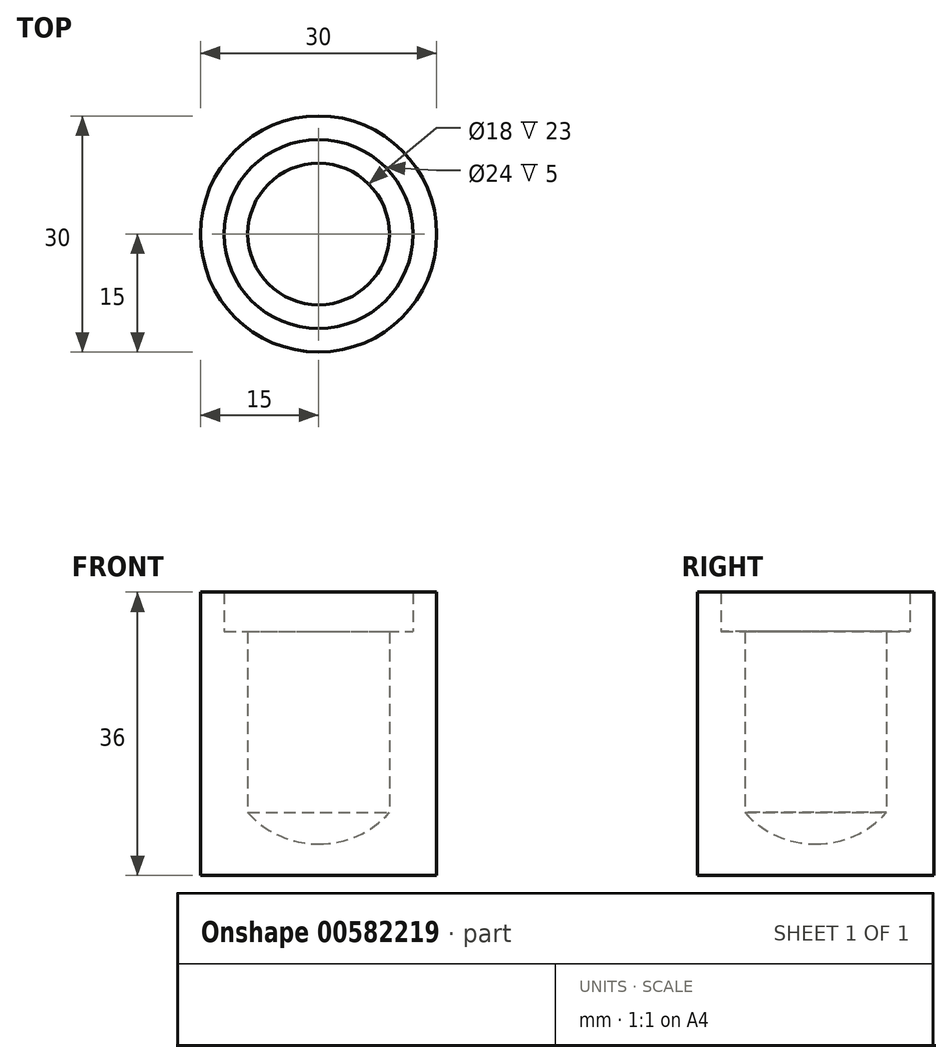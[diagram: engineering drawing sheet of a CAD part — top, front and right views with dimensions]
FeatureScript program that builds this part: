
annotation { "Feature Type Name" : "Feature", "Feature Type Description" : "" }
export const myFeature = defineFeature(function(context is Context, id is Id, definition is map)
    precondition{}
    {
        {
            var Q0;
            Q0=qCreatedBy(makeId("Front.planeOp"),FACE);
            var sketch = newSketch(context, id + "F0", { "sketchPlane" : qUnion([Q0])});
            skLineSegment(sketch, "E0.top", {"start": v(15, -4) * mm, "end": v(-15, -4) * mm});
            skLineSegment(sketch, "E0.left", {"start": v(15, 4) * mm, "end": v(15, -4) * mm});
            skLineSegment(sketch, "E0.right", {"start": v(-15, 4) * mm, "end": v(-15, -4) * mm});
            skPoint(sketch, "E0.middle", {"position": v(0, 0) * mm});
            skLineSegment(sketch, "E1.left", {"start": v(-15, 4) * mm, "end": v(-15, 29) * mm});
            skLineSegment(sketch, "E1.right", {"start": v(-9, 4) * mm, "end": v(-9, 27) * mm});
            skLineSegment(sketch, "E2.left", {"start": v(15, 4) * mm, "end": v(15, 27) * mm});
            skLineSegment(sketch, "E2.right", {"start": v(9, 4) * mm, "end": v(9, 27) * mm});
            skPoint(sketch, "E3.oppositeSnap0", {"position": v(12, 27) * mm});
            skLineSegment(sketch, "E3.top", {"start": v(15, 32) * mm, "end": v(12, 32) * mm});
            skLineSegment(sketch, "E3.left", {"start": v(15, 27) * mm, "end": v(15, 32) * mm});
            skLineSegment(sketch, "E3.right", {"start": v(12, 27) * mm, "end": v(12, 32) * mm});
            skLineSegment(sketch, "E4.top", {"start": v(-15, 32) * mm, "end": v(-12, 32) * mm});
            skLineSegment(sketch, "E4.left", {"start": v(-15, 29) * mm, "end": v(-15, 32) * mm});
            skLineSegment(sketch, "E4.right", {"start": v(-12, 27) * mm, "end": v(-12, 32) * mm});
            skArc(sketch, "E5", {"start": v(-9, 4) * mm, "mid": v(0, 0) * mm, "end": v(9, 4) * mm});
            skLineSegment(sketch, "E6", {"start": v(12, 27) * mm, "end": v(9, 27) * mm});
            skLineSegment(sketch, "E7", {"start": v(-12, 27) * mm, "end": v(-9, 27) * mm});
            skLineSegment(sketch, "E8", {"start": v(0, -4) * mm, "end": v(0, 0) * mm});
            skSolve(sketch);
        }
        {
            var Q0;
            {var subQ1=sQuery(id+"F0.wireOp",EDGE,"E0.right");Q0=makeQuery(id+"F0.imprint","IMPRINT",FACE,{"disambiguationData":[TD([[makeQuery(id+"F0.imprint","IMPRINT",EDGE,{"derivedFrom":subQ1}),1.0]])]});}
            var Q1;
            Q1=sQuery(id+"F0.wireOp",EDGE,"E8");
            revolve(context, id + "F1", {"entities" : qUnion([Q0]), "axis" : qUnion([Q1]), "revolveType" : RevolveType.FULL});
        }
    });
